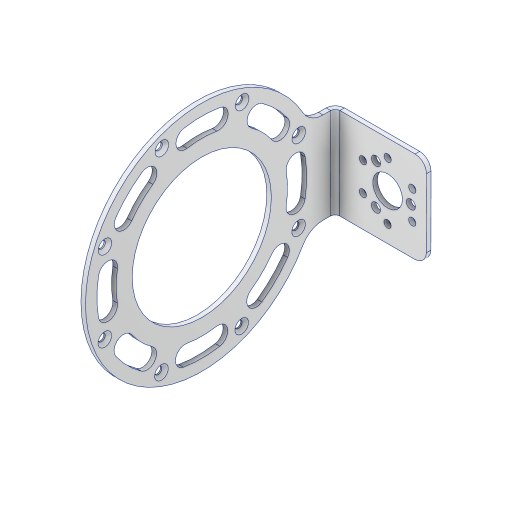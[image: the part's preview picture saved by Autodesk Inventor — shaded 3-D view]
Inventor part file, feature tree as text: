
AUTODESK INVENTOR PART (.ipt)
format: ipt  version: 2023 (Build 270158000, 158)  size: 1,586,688 bytes
history: native  units: mm
features: other x10, sketch x6, extrude x3, fillet x3, hole x1
ambient origin geometry x8: Origin, YZ Plane, XZ Plane, XY Plane, X Axis, Y Axis, Z Axis, Center Point
bodies: Body1 (feature_tree), Body2 (feature_tree)
feature tree (23):
  other  "GIM8108-8_1.ipt"
  other  "ソリッド1"
  other  "フランジ1"
  extrude  "押し出し1"  Depth=10.0mm
  fillet  "フィレット1"  Radius=102.0mm
  fillet  "フィレット2"  Radius=40.0mm
  extrude  "押し出し6"  Depth=20.0mm
  extrude  "押し出し7"  Depth=18.0mm
  fillet  "フィレット3"  Radius=61.0mm
  hole  "穴1"  [1 undecoded]
  other  "TaggingFeature1"
  sketch  "スケッチ1"
  other  "プレート1"
  sketch  "スケッチ2"
  other  "プレート2"
  other  "曲げ1"
  other  "コーナー1"
  sketch  "スケッチ3"
  sketch  "スケッチ7"
  sketch  "スケッチ8"
  sketch  "スケッチ10"
  other  "ソリッド1::GIM8108-8_1.ipt"
  other  "Srf1"
note: 1 required parameter value undecoded (feature->parameter linkage not recoverable at this tier; creation-order binding heuristic only, values carry confidence <= 0.55)
